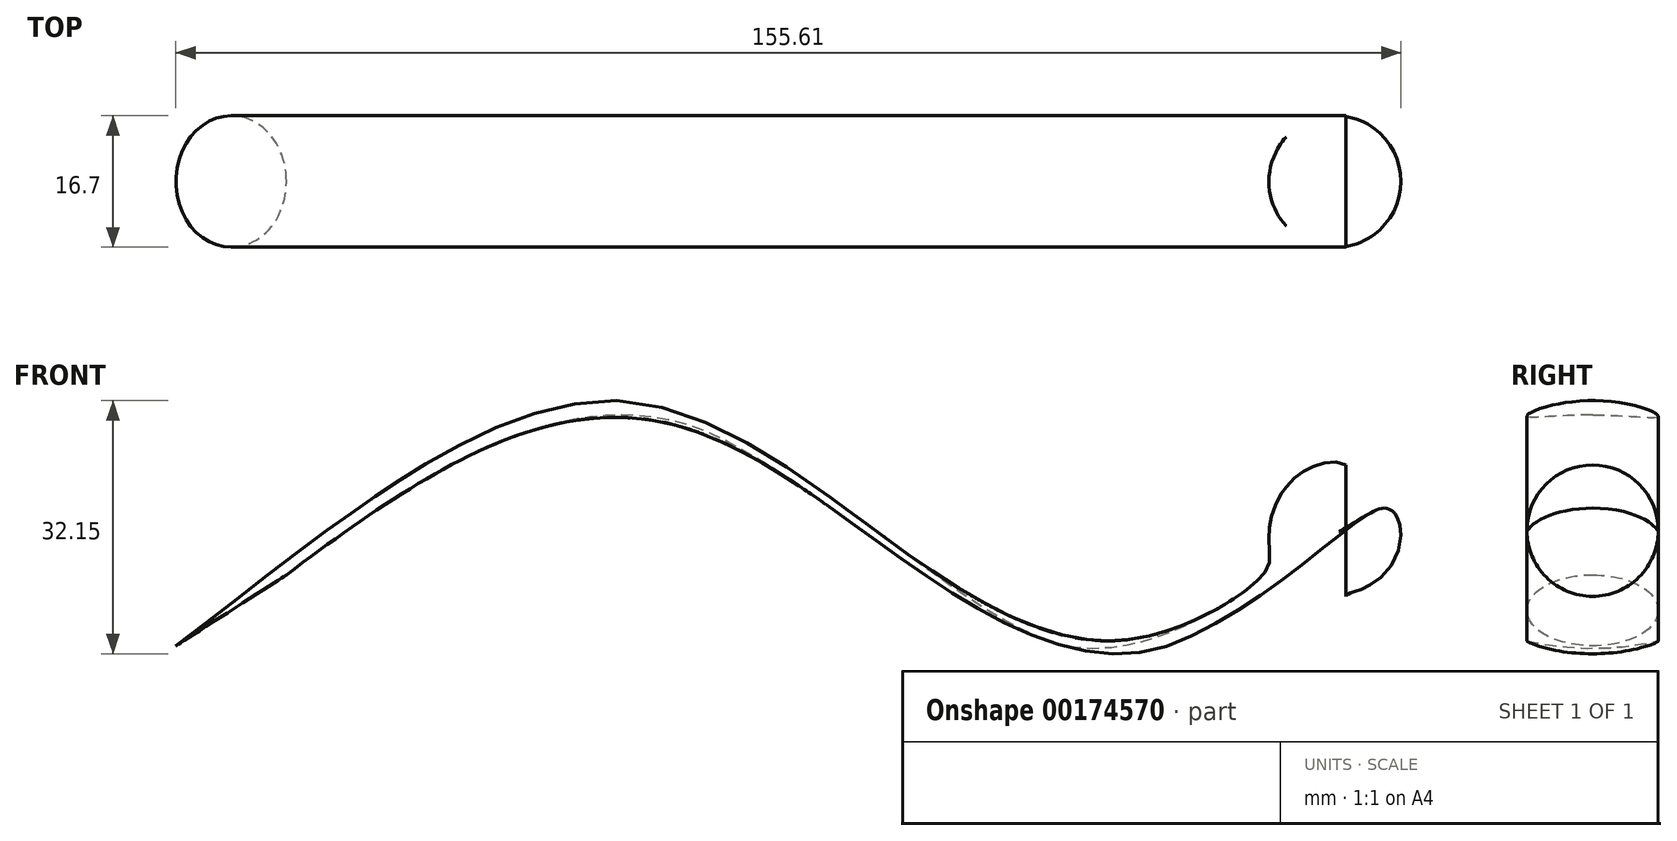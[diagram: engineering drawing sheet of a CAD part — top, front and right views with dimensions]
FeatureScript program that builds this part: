
annotation { "Feature Type Name" : "Feature", "Feature Type Description" : "" }
export const myFeature = defineFeature(function(context is Context, id is Id, definition is map)
    precondition{}
    {
        {
            var Q0;
            Q0=qCreatedBy(makeId("Front.planeOp"),FACE);
            var sketch = newSketch(context, id + "F0", { "sketchPlane" : qUnion([Q0])});
            skFitSpline(sketch, "E0", {"points": [v(-92.8, 25.01) * mm, v(-37.52, 48.27) * mm, v(19.09, 20.62) * mm, v(47.6, 34.67) * mm, v(48.05, 33.79) * mm], "startDerivative": vector(159.1, 120.13) * mm, "endDerivative": vector(2.23, -29.13) * mm});
            skSolve(sketch);
        }
        {
            var Q0;
            Q0=qCreatedBy(makeId("Right.planeOp"),FACE);
            var Q1;
            Q1=sQuery(id+"F0.wireOp",VERTEX,"E0.end");
            cPlane(context, id + "F1", {"entities" : qUnion([Q0, Q1]), "cplaneType" : CPlaneType.PLANE_POINT, "offset" : 25 * mm, "width" : 150 * mm, "height" : 150 * mm});
        }
        {
            var Q0;
            Q0=qCreatedBy(id+"F1.planeOp",FACE);
            var sketch = newSketch(context, id + "F2", { "sketchPlane" : qUnion([Q0])});
            skCircle(sketch, "E1", {"center": v(0, 34.67) * mm, "radius": 8.35 * mm});
            skSolve(sketch);
        }
        {
            var Q0;
            Q0=makeQuery(id+"F2.imprint","IMPRINT",FACE,{"disambiguationData":[TD([[makeQuery(id+"F2.imprint","IMPRINT",EDGE,{"derivedFrom":sQuery(id+"F2.wireOp",EDGE,"E1")}),1.0]])]});
            var Q1;
            Q1=sQuery(id+"F0.wireOp",EDGE,"E0");
            sweep(context, id + "F3", {"profiles" : qUnion([Q0]), "path" : qUnion([Q1])});
        }
    });
